# Revit family: MI-266_041_10
name_source: partatom
category: Plumbing Fixtures
revit_build: Autodesk Revit Architecture 2012 (Build: 20110309_2315(x64)
units: mm (PartAtom-declared; Revit-internal decimal feet)

## types (1)
- MI-266/041/10
    1/2" light pattern tap washer = C-098-15
    Aerator = C-M22X1
    Assembly Code = D2010
    CW Connection = Yes
    CWFU = 0
    Concealled connections = S-050L-20X15
    Cost = 0 $
    Default Elevation = 0' - 0"
    Description = Wall type with aerated swivel outlet. 1/2"BSP male inlets
    HW Connection = Yes
    HWFU = 0
    Keynote = Sink mixer with aerated swivel outlet
    Manufacturer = COBRA
    Material = Chrome - Polished
    Model = MI-266/041/10
    Range = Metsi
    Swivel outlet = S-041/10
    Type Comments = SANS 226 TYPE 2
    URL = http://www.cobra.co.za
    Vent Connection = No
    WFU = 0
    Waste Connection = No

## geometry (parser evidence)
native form markers: Blend x2
no freeform markers — native parametric forms only
